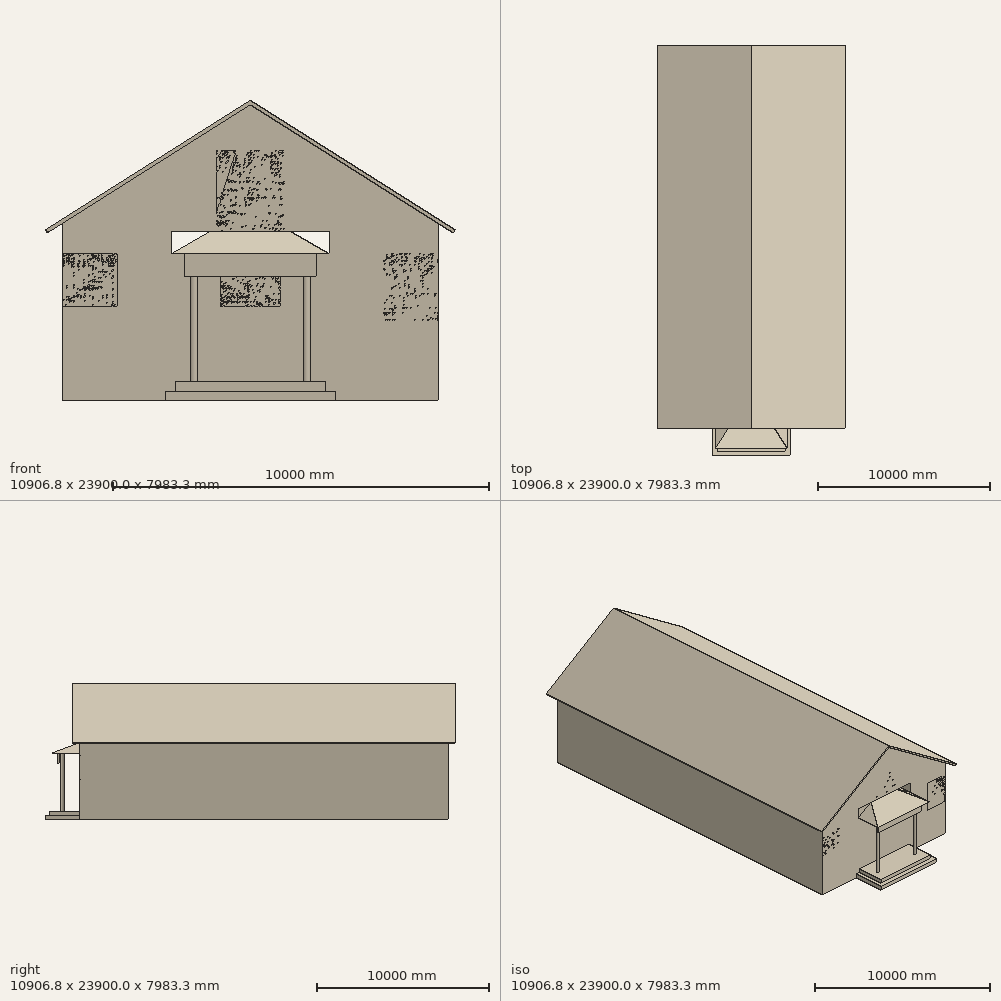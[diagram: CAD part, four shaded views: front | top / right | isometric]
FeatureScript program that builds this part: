
annotation { "Feature Type Name" : "Feature", "Feature Type Description" : "" }
export const myFeature = defineFeature(function(context is Context, id is Id, definition is map)
    precondition{}
    {
        {
            var Q0;
            Q0=qCreatedBy(makeId("Front.planeOp"),FACE);
            var sketch = newSketch(context, id + "F0", { "sketchPlane" : qUnion([Q0])});
            skLineSegment(sketch, "E0", {"start": v(0, 0) * mm, "end": v(0, 7865) * mm});
            skLineSegment(sketch, "E1", {"start": v(0, 7865) * mm, "end": v(5000, 4705) * mm});
            skLineSegment(sketch, "E2", {"start": v(5000, 4705) * mm, "end": v(5000, 0) * mm});
            skLineSegment(sketch, "E3", {"start": v(5000, 0) * mm, "end": v(0, 0) * mm});
            skSolve(sketch);
        }
        {
            var Q0;
            Q0=makeQuery(id+"F0.imprint","IMPRINT",FACE,{"disambiguationData":[TD([[makeQuery(id+"F0.imprint","IMPRINT",EDGE,{"derivedFrom":sQuery(id+"F0.wireOp",EDGE,"E0")}),-1.0]])]});
            extrude(context, id + "F1", {"entities" : qUnion([Q0]), "endBound" : BoundingType.SYMMETRIC, "depth" : 21500 * mm});
        }
        {
            var Q0;
            Q0=makeQuery(id+"F1.opExtrude","CAP_FACE",FACE,{"disambiguationData":[OSD([sQuery(id+"F0.wireOp",EDGE,"E0"),sQuery(id+"F0.wireOp",EDGE,"E1"),sQuery(id+"F0.wireOp",EDGE,"E2"),sQuery(id+"F0.wireOp",EDGE,"E3")])],"isStart":false});
            var sketch = newSketch(context, id + "F2", { "sketchPlane" : qUnion([Q0])});
            skLineSegment(sketch, "E4", {"start": v(5453.42, 4536.73) * mm, "end": v(5400, 4452.2) * mm});
            skLineSegment(sketch, "E5", {"start": v(5400, 4452.2) * mm, "end": v(0, 7865) * mm});
            skLineSegment(sketch, "E6", {"start": v(0, 7983.3) * mm, "end": v(5453.42, 4536.73) * mm});
            skLineSegment(sketch, "E7", {"start": v(0, 7865) * mm, "end": v(0, 7983.3) * mm});
            skSolve(sketch);
        }
        {
            var Q0;
            Q0=qSketchRegion(id+"F2",true);
            extrude(context, id + "F3", {"entities" : qUnion([Q0]), "oppositeDirection" : true, "depth" : 21500 * mm});
        }
        {
            var Q0;
            Q0=makeQuery(id+"F3.opExtrude","CAP_FACE",FACE,{"disambiguationData":[OSD([sQuery(id+"F2.wireOp",EDGE,"E4"),sQuery(id+"F2.wireOp",EDGE,"E5"),sQuery(id+"F2.wireOp",EDGE,"E6"),sQuery(id+"F2.wireOp",EDGE,"E7")])],"isStart":true});
            var sketch = newSketch(context, id + "F4", { "sketchPlane" : qUnion([Q0])});
            skLineSegment(sketch, "E8.0", {"start": v(0, 7983.3) * mm, "end": v(5453.42, 4536.73) * mm});
            skLineSegment(sketch, "E9.0", {"start": v(5453.42, 4536.73) * mm, "end": v(5400, 4452.2) * mm});
            skLineSegment(sketch, "E10.0", {"start": v(0, 7865) * mm, "end": v(5400, 4452.2) * mm});
            skLineSegment(sketch, "E11.0", {"start": v(0, 7865) * mm, "end": v(0, 7983.3) * mm});
            skSolve(sketch);
        }
        {
            var Q0;
            Q0=makeQuery(id+"F4.imprint","IMPRINT",FACE,{"disambiguationData":[TD([[makeQuery(id+"F4.imprint","IMPRINT",EDGE,{"derivedFrom":sQuery(id+"F4.wireOp",EDGE,"E8.0")}),-1.0]])]});
            extrude(context, id + "F5", {"entities" : qUnion([Q0]), "operationType" : NewBodyOperationType.ADD, "depth" : 400 * mm});
        }
        {
            var Q0;
            Q0=makeQuery(id+"F3.opExtrude","CAP_FACE",FACE,{"disambiguationData":[OSD([sQuery(id+"F2.wireOp",EDGE,"E4"),sQuery(id+"F2.wireOp",EDGE,"E5"),sQuery(id+"F2.wireOp",EDGE,"E6"),sQuery(id+"F2.wireOp",EDGE,"E7")])],"isStart":false});
            var sketch = newSketch(context, id + "F6", { "sketchPlane" : qUnion([Q0])});
            skLineSegment(sketch, "E12.0", {"start": v(0, 7983.3) * mm, "end": v(-5453.42, 4536.73) * mm});
            skLineSegment(sketch, "E13.0", {"start": v(0, 7865) * mm, "end": v(-5000, 4705) * mm});
            skLineSegment(sketch, "E14.0", {"start": v(0, 7865) * mm, "end": v(-5400, 4452.2) * mm});
            skLineSegment(sketch, "E15.0", {"start": v(-5453.42, 4536.73) * mm, "end": v(-5400, 4452.2) * mm});
            skLineSegment(sketch, "E16.0", {"start": v(0, 7865) * mm, "end": v(0, 7983.3) * mm});
            skSolve(sketch);
        }
        {
            var Q0;
            Q0=makeQuery(id+"F6.imprint","IMPRINT",FACE,{"disambiguationData":[TD([[makeQuery(id+"F6.imprint","IMPRINT",EDGE,{"derivedFrom":sQuery(id+"F6.wireOp",EDGE,"E12.0")}),1.0]])]});
            extrude(context, id + "F7", {"entities" : qUnion([Q0]), "operationType" : NewBodyOperationType.ADD, "depth" : 400 * mm});
        }
        {
            var Q0;
            Q0=makeQuery(id+"F1.opExtrude","SWEPT_BODY",BODY,{"disambiguationData":[OSD([sQuery(id+"F0.wireOp",EDGE,"E0"),sQuery(id+"F0.wireOp",EDGE,"E1"),sQuery(id+"F0.wireOp",EDGE,"E2"),sQuery(id+"F0.wireOp",EDGE,"E3")])]});
            var Q1;
            Q1=makeQuery(id+"F3.opExtrude","SWEPT_BODY",BODY,{"disambiguationData":[OSD([sQuery(id+"F2.wireOp",EDGE,"E4"),sQuery(id+"F2.wireOp",EDGE,"E5"),sQuery(id+"F2.wireOp",EDGE,"E6"),sQuery(id+"F2.wireOp",EDGE,"E7")])]});
            var Q2;
            Q2=makeQuery(id+"F1.opExtrude","SWEPT_FACE",FACE,{"disambiguationData":[OSD([sQuery(id+"F0.wireOp",EDGE,"E0")])]});
            mirror(context, id + "F8", {"operationType" : NewBodyOperationType.ADD, "entities" : qUnion([Q0, Q1]), "mirrorPlane" : qUnion([Q2])});
        }
        {
            var Q0;
            {var subQ0=makeQuery(id+"F1.opExtrude","CAP_FACE",FACE,{"disambiguationData":[OSD([sQuery(id+"F0.wireOp",EDGE,"E0"),sQuery(id+"F0.wireOp",EDGE,"E1"),sQuery(id+"F0.wireOp",EDGE,"E2"),sQuery(id+"F0.wireOp",EDGE,"E3")])],"isStart":false});Q0=makeQuery(id+"F8.boolean.opBoolean","MERGE",FACE,{"derivedFrom":[subQ0,makeQuery(id+"F8.opPattern","COPY",FACE,{"derivedFrom":subQ0,"instanceName":"1"})]});}
            var sketch = newSketch(context, id + "F9", { "sketchPlane" : qUnion([Q0])});
            skLineSegment(sketch, "E17.bottom", {"start": v(-5000, 2500) * mm, "end": v(-3530, 2500) * mm});
            skLineSegment(sketch, "E17.top", {"start": v(-5000, 3900) * mm, "end": v(-3530, 3900) * mm});
            skLineSegment(sketch, "E17.left", {"start": v(-5000, 2500) * mm, "end": v(-5000, 3900) * mm});
            skLineSegment(sketch, "E17.right", {"start": v(-3530, 2500) * mm, "end": v(-3530, 3900) * mm});
            skLineSegment(sketch, "E18.bottom", {"start": v(-785, 2500) * mm, "end": v(785, 2500) * mm});
            skLineSegment(sketch, "E18.top", {"start": v(-785, 3900) * mm, "end": v(785, 3900) * mm});
            skLineSegment(sketch, "E18.left", {"start": v(-785, 2500) * mm, "end": v(-785, 3900) * mm});
            skLineSegment(sketch, "E18.right", {"start": v(785, 2500) * mm, "end": v(785, 3900) * mm});
            skLineSegment(sketch, "E19.bottom", {"start": v(3530, 2100) * mm, "end": v(5000, 2100) * mm});
            skLineSegment(sketch, "E19.top", {"start": v(3530, 3900) * mm, "end": v(5000, 3900) * mm});
            skLineSegment(sketch, "E19.left", {"start": v(3530, 2100) * mm, "end": v(3530, 3900) * mm});
            skLineSegment(sketch, "E19.right", {"start": v(5000, 2100) * mm, "end": v(5000, 3900) * mm});
            skLineSegment(sketch, "E20.bottom", {"start": v(-900, 6652) * mm, "end": v(900, 6652) * mm});
            skLineSegment(sketch, "E20.top", {"start": v(-900, 4502) * mm, "end": v(900, 4502) * mm});
            skLineSegment(sketch, "E20.left", {"start": v(-900, 6652) * mm, "end": v(-900, 4502) * mm});
            skLineSegment(sketch, "E20.right", {"start": v(900, 6652) * mm, "end": v(900, 4502) * mm});
            skLineSegment(sketch, "E21.0", {"start": v(-5000, 4705) * mm, "end": v(-5000, 0) * mm});
            skPoint(sketch, "E22", {"position": v(0, 2500) * mm});
            skPoint(sketch, "E23.0", {"position": v(0, 0) * mm});
            skPoint(sketch, "E24", {"position": v(0, 4502) * mm});
            skSolve(sketch);
        }
        {
            var Q0;
            Q0=makeQuery(id+"F9.imprint","IMPRINT",FACE,{"disambiguationData":[TD([[makeQuery(id+"F9.imprint","IMPRINT",EDGE,{"derivedFrom":sQuery(id+"F9.wireOp",EDGE,"E20.bottom")}),-1.0]])]});
            var Q1;
            Q1=makeQuery(id+"F9.imprint","IMPRINT",FACE,{"disambiguationData":[TD([[makeQuery(id+"F9.imprint","IMPRINT",EDGE,{"derivedFrom":sQuery(id+"F9.wireOp",EDGE,"E18.bottom")}),1.0]])]});
            var Q2;
            {var subQ0=sQuery(id+"F9.wireOp",EDGE,"E17.bottom");Q2=makeQuery(id+"F9.imprint","IMPRINT",FACE,{"disambiguationData":[TD([[makeQuery(id+"F9.imprint","IMPRINT",EDGE,{"derivedFrom":subQ0}),1.0]])]});}
            var Q3;
            Q3=makeQuery(id+"F9.imprint","IMPRINT",FACE,{"disambiguationData":[TD([[makeQuery(id+"F9.imprint","IMPRINT",EDGE,{"derivedFrom":sQuery(id+"F9.wireOp",EDGE,"E19.bottom")}),1.0]])]});
            extrude(context, id + "F10", {"entities" : qUnion([Q0, Q1, Q2, Q3]), "oppositeDirection" : true, "depth" : 25 * mm});
        }
        {
            var Q0;
            Q0=qCreatedBy(makeId("Top.planeOp"),FACE);
            var sketch = newSketch(context, id + "F11", { "sketchPlane" : qUnion([Q0])});
            skLineSegment(sketch, "E25.0", {"start": v(5000, -10750) * mm, "end": v(-5000, -10750) * mm});
            skLineSegment(sketch, "E26", {"start": v(0, -10750) * mm, "end": v(0, -11750) * mm, "construction": true});
            skCircle(sketch, "E27", {"center": v(-1500, -11750) * mm, "radius": 100 * mm});
            skCircle(sketch, "E28", {"center": v(1500, -11750) * mm, "radius": 100 * mm});
            skLineSegment(sketch, "E29", {"start": v(-1500, -11750) * mm, "end": v(1500, -11750) * mm, "construction": true});
            skPoint(sketch, "E30", {"position": v(0, -11750) * mm});
            skSolve(sketch);
        }
        {
            var Q0;
            Q0=makeQuery(id+"F11.imprint","IMPRINT",FACE,{"disambiguationData":[TD([[makeQuery(id+"F11.imprint","IMPRINT",EDGE,{"derivedFrom":sQuery(id+"F11.wireOp",EDGE,"E27")}),1.0]])]});
            var Q1;
            Q1=makeQuery(id+"F11.imprint","IMPRINT",FACE,{"disambiguationData":[TD([[makeQuery(id+"F11.imprint","IMPRINT",EDGE,{"derivedFrom":sQuery(id+"F11.wireOp",EDGE,"E28")}),1.0]])]});
            extrude(context, id + "F12", {"entities" : qUnion([Q0, Q1]), "depth" : 3900 * mm});
        }
        {
            var Q0;
            Q0=makeQuery(id+"F12.opExtrude","CAP_FACE",FACE,{"disambiguationData":[OSD([sQuery(id+"F11.wireOp",EDGE,"E27")])],"isStart":false});
            var sketch = newSketch(context, id + "F13", { "sketchPlane" : qUnion([Q0])});
            skLineSegment(sketch, "E31", {"start": v(-2100, -10750) * mm, "end": v(-2100, -12350) * mm});
            skLineSegment(sketch, "E32", {"start": v(-2100, -12350) * mm, "end": v(2100, -12350) * mm});
            skLineSegment(sketch, "E33", {"start": v(2100, -12350) * mm, "end": v(2100, -10750) * mm});
            skLineSegment(sketch, "E34.0", {"start": v(2100, -10750) * mm, "end": v(-2100, -10750) * mm});
            skCircle(sketch, "E35.0", {"center": v(1500, -11750) * mm, "radius": 100 * mm});
            skCircle(sketch, "E36.0", {"center": v(-1500, -11750) * mm, "radius": 100 * mm});
            skPoint(sketch, "E37.orphan", {"position": v(5000, -10750) * mm});
            skPoint(sketch, "E38.orphan", {"position": v(-5000, -10750) * mm});
            skSolve(sketch);
        }
        {
            var Q0;
            Q0=qSketchRegion(id+"F13",true);
            var Q1;
            Q1=makeQuery(id+"F13.imprint","IMPRINT",FACE,{"disambiguationData":[TD([[makeQuery(id+"F13.imprint","IMPRINT",EDGE,{"derivedFrom":sQuery(id+"F13.wireOp",EDGE,"E35.0")}),1.0]])]});
            var Q2;
            Q2=makeQuery(id+"F13.imprint","IMPRINT",FACE,{"disambiguationData":[TD([[makeQuery(id+"F13.imprint","IMPRINT",EDGE,{"derivedFrom":sQuery(id+"F13.wireOp",EDGE,"E36.0")}),1.0]])]});
            extrude(context, id + "F14", {"entities" : qUnion([Q0, Q1, Q2]), "depth" : 600 * mm});
        }
        {
            var Q0;
            Q0=makeQuery(id+"F14.opExtrude","SWEPT_FACE",FACE,{"disambiguationData":[OSD([sQuery(id+"F13.wireOp",EDGE,"E33")])]});
            var sketch = newSketch(context, id + "F15", { "sketchPlane" : qUnion([Q0])});
            skLineSegment(sketch, "E39", {"start": v(-12350, 3900) * mm, "end": v(-10750, 4500) * mm});
            skSolve(sketch);
        }
        {
            var Q0;
            Q0=makeQuery(id+"F15.imprint","IMPRINT",FACE,{"disambiguationData":[TD([[makeQuery(id+"F15.imprint","IMPRINT",EDGE,{"derivedFrom":sQuery(id+"F15.wireOp",EDGE,"E39")}),1.0]])]});
            extrude(context, id + "F16", {"entities" : qUnion([Q0]), "operationType" : NewBodyOperationType.REMOVE, "endBound" : BoundingType.THROUGH_ALL, "oppositeDirection" : true, "depth" : 25 * mm});
        }
        {
            var Q0;
            {var subQ0=makeQuery(id+"F1.opExtrude","CAP_FACE",FACE,{"disambiguationData":[OSD([sQuery(id+"F0.wireOp",EDGE,"E0"),sQuery(id+"F0.wireOp",EDGE,"E1"),sQuery(id+"F0.wireOp",EDGE,"E2"),sQuery(id+"F0.wireOp",EDGE,"E3")])],"isStart":false});Q0=makeQuery(id+"F8.boolean.opBoolean","MERGE",FACE,{"derivedFrom":[subQ0,makeQuery(id+"F8.opPattern","COPY",FACE,{"derivedFrom":subQ0,"instanceName":"1"})]});}
            cPlane(context, id + "F17", {"entities" : qUnion([Q0]), "cplaneType" : CPlaneType.OFFSET, "offset" : 2000 * mm, "width" : 150 * mm, "height" : 150 * mm});
        }
        {
            var Q0;
            Q0=qCreatedBy(id+"F17.planeOp",FACE);
            var sketch = newSketch(context, id + "F18", { "sketchPlane" : qUnion([Q0])});
            skLineSegment(sketch, "E40.0", {"start": v(2100, 4500) * mm, "end": v(-2100, 4500) * mm});
            skLineSegment(sketch, "E40.1", {"start": v(-2100, 3900) * mm, "end": v(2100, 3900) * mm});
            skLineSegment(sketch, "E41", {"start": v(2100, 3900) * mm, "end": v(1060.77, 4500) * mm});
            skLineSegment(sketch, "E42", {"start": v(2100, 3900) * mm, "end": v(2100, 4500) * mm});
            skLineSegment(sketch, "E43", {"start": v(-2100, 3900) * mm, "end": v(-2100, 4500) * mm});
            skLineSegment(sketch, "E44", {"start": v(-2100, 3900) * mm, "end": v(-1060.77, 4500) * mm});
            skSolve(sketch);
        }
        {
            var Q0;
            {var subQ0=sQuery(id+"F18.wireOp",EDGE,"E43");Q0=makeQuery(id+"F18.imprint","IMPRINT",FACE,{"disambiguationData":[TD([[makeQuery(id+"F18.imprint","IMPRINT",EDGE,{"derivedFrom":subQ0}),-1.0]])]});}
            var Q1;
            {var subQ2=sQuery(id+"F18.wireOp",EDGE,"E41");Q1=makeQuery(id+"F18.imprint","IMPRINT",FACE,{"disambiguationData":[TD([[makeQuery(id+"F18.imprint","IMPRINT",EDGE,{"derivedFrom":subQ2}),-1.0]])]});}
            extrude(context, id + "F19", {"entities" : qUnion([Q0, Q1]), "operationType" : NewBodyOperationType.REMOVE, "endBound" : BoundingType.THROUGH_ALL, "oppositeDirection" : true, "depth" : 25 * mm});
        }
        {
            var Q0;
            {var subQ0=makeQuery(id+"F1.opExtrude","CAP_FACE",FACE,{"disambiguationData":[OSD([sQuery(id+"F0.wireOp",EDGE,"E0"),sQuery(id+"F0.wireOp",EDGE,"E1"),sQuery(id+"F0.wireOp",EDGE,"E2"),sQuery(id+"F0.wireOp",EDGE,"E3")])],"isStart":false});Q0=makeQuery(id+"F8.boolean.opBoolean","MERGE",FACE,{"derivedFrom":[subQ0,makeQuery(id+"F8.opPattern","COPY",FACE,{"derivedFrom":subQ0,"instanceName":"1"})]});}
            var sketch = newSketch(context, id + "F20", { "sketchPlane" : qUnion([Q0])});
            skLineSegment(sketch, "E45", {"start": v(-2250, 0) * mm, "end": v(-2250, 250) * mm});
            skLineSegment(sketch, "E46", {"start": v(-2250, 250) * mm, "end": v(-2000, 250) * mm});
            skLineSegment(sketch, "E47", {"start": v(-2000, 250) * mm, "end": v(-2000, 500) * mm});
            skLineSegment(sketch, "E48", {"start": v(-2000, 500) * mm, "end": v(2000, 500) * mm});
            skLineSegment(sketch, "E49", {"start": v(2000, 500) * mm, "end": v(2000, 250) * mm});
            skLineSegment(sketch, "E50", {"start": v(2000, 250) * mm, "end": v(2250, 250) * mm});
            skLineSegment(sketch, "E51", {"start": v(2250, 250) * mm, "end": v(2250, 0) * mm});
            skPoint(sketch, "E52", {"position": v(0, 500) * mm});
            skSolve(sketch);
        }
        {
            var Q0;
            {var subQ0=sQuery(id+"F20.wireOp",EDGE,"E45");Q0=makeQuery(id+"F20.imprint","IMPRINT",FACE,{"disambiguationData":[TD([[makeQuery(id+"F20.imprint","IMPRINT",EDGE,{"derivedFrom":subQ0}),-1.0]])]});}
            extrude(context, id + "F21", {"entities" : qUnion([Q0]), "depth" : 2000 * mm});
        }
        {
            var Q0;
            Q0=makeQuery(id+"F21.opExtrude","CAP_FACE",FACE,{"disambiguationData":[OSD([sQuery(id+"F0.wireOp",EDGE,"E3"),sQuery(id+"F20.wireOp",EDGE,"E45"),sQuery(id+"F20.wireOp",EDGE,"E46"),sQuery(id+"F20.wireOp",EDGE,"E47"),sQuery(id+"F20.wireOp",EDGE,"E48"),sQuery(id+"F20.wireOp",EDGE,"E49"),sQuery(id+"F20.wireOp",EDGE,"E50"),sQuery(id+"F20.wireOp",EDGE,"E51")])],"isStart":false});
            var sketch = newSketch(context, id + "F22", { "sketchPlane" : qUnion([Q0])});
            skLineSegment(sketch, "E53", {"start": v(-2000, 250) * mm, "end": v(2000, 250) * mm});
            skSolve(sketch);
        }
        {
            var Q0;
            Q0=makeQuery(id+"F22.imprint","IMPRINT",FACE,{"disambiguationData":[TD([[makeQuery(id+"F22.imprint","IMPRINT",EDGE,{"derivedFrom":sQuery(id+"F22.wireOp",EDGE,"E53")}),1.0]])]});
            extrude(context, id + "F23", {"entities" : qUnion([Q0]), "operationType" : NewBodyOperationType.REMOVE, "oppositeDirection" : true, "depth" : 250 * mm});
        }
        {
            var Q0;
            Q0=makeQuery(id+"F13.imprint","IMPRINT",FACE,{"disambiguationData":[TD([[makeQuery(id+"F13.imprint","IMPRINT",EDGE,{"derivedFrom":sQuery(id+"F13.wireOp",EDGE,"E31")}),1.0]])]});
            var sketch = newSketch(context, id + "F24", { "sketchPlane" : qUnion([Q0])});
            skCircle(sketch, "E54.0", {"center": v(-1500, -11750) * mm, "radius": 100 * mm});
            skCircle(sketch, "E55.0", {"center": v(1500, -11750) * mm, "radius": 100 * mm});
            skLineSegment(sketch, "E56.bottom", {"start": v(-1750, -12050) * mm, "end": v(1750, -12050) * mm});
            skLineSegment(sketch, "E56.top", {"start": v(-1750, -11950) * mm, "end": v(1750, -11950) * mm});
            skLineSegment(sketch, "E56.left", {"start": v(-1750, -12050) * mm, "end": v(-1750, -11950) * mm});
            skLineSegment(sketch, "E56.right", {"start": v(1750, -12050) * mm, "end": v(1750, -11950) * mm});
            skPoint(sketch, "E57", {"position": v(0, -11950) * mm});
            skSolve(sketch);
        }
        {
            var Q0;
            Q0=makeQuery(id+"F24.imprint","IMPRINT",FACE,{"disambiguationData":[TD([[makeQuery(id+"F24.imprint","IMPRINT",EDGE,{"derivedFrom":sQuery(id+"F24.wireOp",EDGE,"E56.bottom")}),1.0]])]});
            extrude(context, id + "F25", {"entities" : qUnion([Q0]), "oppositeDirection" : true, "depth" : 600 * mm});
        }
    });
